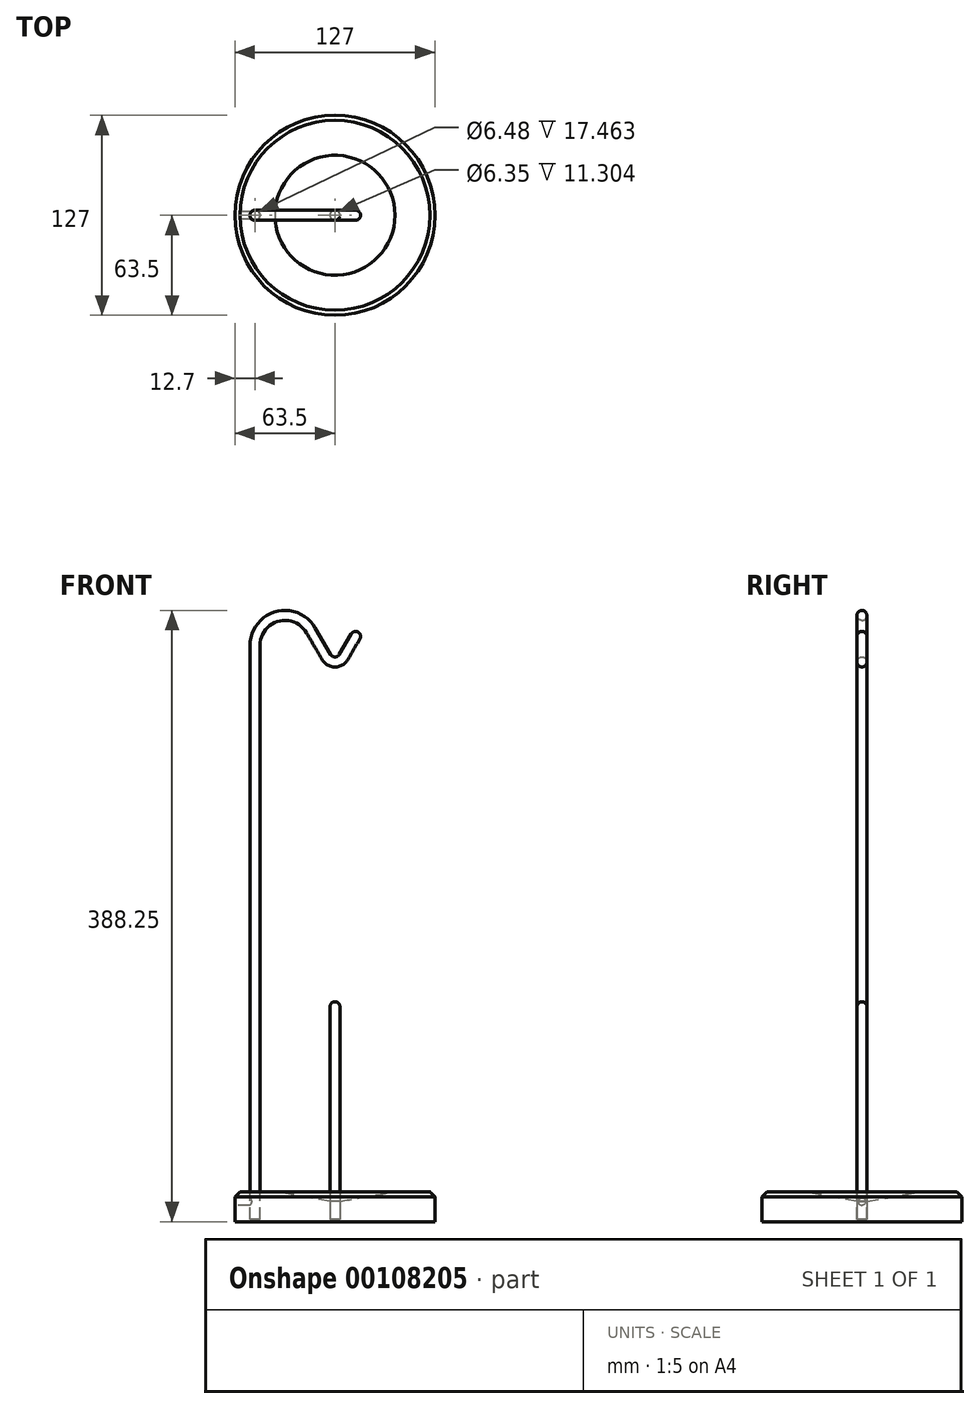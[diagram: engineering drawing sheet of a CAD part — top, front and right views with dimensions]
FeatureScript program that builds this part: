
annotation { "Feature Type Name" : "Feature", "Feature Type Description" : "" }
export const myFeature = defineFeature(function(context is Context, id is Id, definition is map)
    precondition{}
    {
        {
            var Q0;
            Q0=qCreatedBy(makeId("Front.planeOp"),FACE);
            var sketch = newSketch(context, id + "F0", { "sketchPlane" : qUnion([Q0])});
            skLineSegment(sketch, "E0", {"start": v(0, 0) * mm, "end": v(-63.5, 0) * mm});
            skLineSegment(sketch, "E1", {"start": v(-63.5, 0) * mm, "end": v(-63.5, 15.88) * mm});
            skLineSegment(sketch, "E2", {"start": v(-60.33, 19.05) * mm, "end": v(0, 19.05) * mm});
            skLineSegment(sketch, "E3", {"start": v(0, 19.05) * mm, "end": v(0, 0) * mm});
            skLineSegment(sketch, "E4", {"start": v(0, 12.33) * mm, "end": v(-38.1, 19.05) * mm});
            skLineSegment(sketch, "E5", {"start": v(0, 43.2) * mm, "end": v(0, -28.1) * mm, "construction": true});
            skPoint(sketch, "E5.endSnap0", {"position": v(0, 9.52) * mm});
            skLineSegment(sketch, "E6", {"start": v(-50.8, 40.56) * mm, "end": v(-50.8, -18.61) * mm, "construction": true});
            skLineSegment(sketch, "E7", {"start": v(-3.18, 19.05) * mm, "end": v(-3.17, 0) * mm, "construction": true});
            skLineSegment(sketch, "E8", {"start": v(-63.5, 15.88) * mm, "end": v(-60.33, 19.05) * mm});
            skLineSegment(sketch, "E9", {"start": v(-63.5, 0) * mm, "end": v(-63.5, 34.42) * mm, "construction": true});
            skSolve(sketch);
        }
        {
            var Q0;
            Q0=makeQuery(id+"F0.imprint","IMPRINT",FACE,{"disambiguationData":[TD([[makeQuery(id+"F0.imprint","IMPRINT",EDGE,{"derivedFrom":sQuery(id+"F0.wireOp",EDGE,"E0")}),-1.0]])]});
            var Q1;
            Q1=sQuery(id+"F0.wireOp",EDGE,"E3");
            revolve(context, id + "F1", {"entities" : qUnion([Q0]), "axis" : qUnion([Q1]), "revolveType" : RevolveType.FULL});
        }
        {
            var Q0;
            Q0=makeQuery(id+"F1.opRevolve","SWEPT_FACE",FACE,{"disambiguationData":[OSD([sQuery(id+"F0.wireOp",EDGE,"E2")])]});
            var sketch = newSketch(context, id + "F2", { "sketchPlane" : qUnion([Q0])});
            skLineSegment(sketch, "E10", {"start": v(81.4, 0) * mm, "end": v(-78.6, 0) * mm, "construction": true});
            skCircle(sketch, "E11", {"center": v(-50.8, 0) * mm, "radius": 3.24 * mm});
            skSolve(sketch);
        }
        {
            var Q0;
            Q0=makeQuery(id+"F2.imprint","IMPRINT",FACE,{"disambiguationData":[TD([[makeQuery(id+"F2.imprint","IMPRINT",EDGE,{"derivedFrom":sQuery(id+"F2.wireOp",EDGE,"E11")}),1.0]])]});
            extrude(context, id + "F3", {"entities" : qUnion([Q0]), "operationType" : NewBodyOperationType.REMOVE, "oppositeDirection" : true, "depth" : 17.46 * mm});
        }
        {
            var Q0;
            Q0=qCreatedBy(makeId("Top.planeOp"),FACE);
            var sketch = newSketch(context, id + "F4", { "sketchPlane" : qUnion([Q0])});
            skCircle(sketch, "E12", {"center": v(0, 0) * mm, "radius": 3.18 * mm});
            skSolve(sketch);
        }
        {
            var Q0;
            Q0 = qSketchRegion(id + "F4", true);
            extrude(context, id + "F5", {"entities" : qUnion([Q0]), "operationType" : NewBodyOperationType.REMOVE, "depth" : 15.24 * mm, "hasSecondDirection" : true, "secondDirectionOppositeDirection" : false, "secondDirectionDepth" : 1.59 * mm});
        }
        {
            var Q0;
            Q0=qCreatedBy(makeId("Top.planeOp"),FACE);
            var sketch = newSketch(context, id + "F6", { "sketchPlane" : qUnion([Q0])});
            skCircle(sketch, "E13", {"center": v(0, 0.01) * mm, "radius": 3.18 * mm});
            skSolve(sketch);
        }
        {
            var Q0;
            Q0 = qSketchRegion(id + "F6", true);
            extrude(context, id + "F7", {"entities" : qUnion([Q0]), "depth" : 139.7 * mm, "hasSecondDirection" : true, "secondDirectionOppositeDirection" : false, "secondDirectionDepth" : 1.59 * mm});
        }
        {
            var Q0;
            Q0=qCreatedBy(makeId("Right.planeOp"),FACE);
            cPlane(context, id + "F8", {"entities" : qUnion([Q0]), "cplaneType" : CPlaneType.OFFSET, "offset" : 63.5 * mm, "oppositeDirection" : true, "width" : 152.4 * mm, "height" : 152.4 * mm});
        }
        {
            var Q0;
            Q0=qCreatedBy(id+"F8.planeOp",FACE);
            var sketch = newSketch(context, id + "F9", { "sketchPlane" : qUnion([Q0])});
            skCircle(sketch, "E14", {"center": v(0, 12.7) * mm, "radius": 2.38 * mm});
            skSolve(sketch);
        }
        {
            var Q0;
            Q0 = qSketchRegion(id + "F9", true);
            extrude(context, id + "F10", {"entities" : qUnion([Q0]), "operationType" : NewBodyOperationType.REMOVE, "depth" : 12.7 * mm});
        }
        {
            var Q0;
            Q0=qCreatedBy(makeId("Front.planeOp"),FACE);
            var sketch = newSketch(context, id + "F11", { "sketchPlane" : qUnion([Q0])});
            skLineSegment(sketch, "E15", {"start": v(-50.8, 1.59) * mm, "end": v(-50.8, 366.03) * mm});
            skLineSegment(sketch, "E16", {"start": v(5.5, 358.66) * mm, "end": v(14.66, 374.54) * mm});
            skLineSegment(sketch, "E17", {"start": v(-5.5, 358.66) * mm, "end": v(-15.25, 375.55) * mm});
            skPoint(sketch, "E18.visualSharp", {"position": v(0, 349.14) * mm});
            skArc(sketch, "E18.filletArc", {"start": v(-5.5, 358.66) * mm, "mid": v(0, 355.49) * mm, "end": v(5.5, 358.66) * mm});
            skPoint(sketch, "E19.visualSharp", {"position": v(-50.8, 437.12) * mm});
            skArc(sketch, "E19.filletArc", {"start": v(-15.25, 375.55) * mm, "mid": v(-36.68, 384.43) * mm, "end": v(-50.8, 366.03) * mm});
            skSolve(sketch);
        }
        {
            var Q0;
            Q0=makeQuery(id+"F3.boolean.opBoolean","COPY",FACE,{"derivedFrom":makeQuery(id+"F3.opExtrude","CAP_FACE",FACE,{"disambiguationData":[OSD([sQuery(id+"F2.wireOp",EDGE,"E11")])],"isStart":false})});
            var sketch = newSketch(context, id + "F12", { "sketchPlane" : qUnion([Q0])});
            skCircle(sketch, "E20", {"center": v(-50.8, 0) * mm, "radius": 3.18 * mm});
            skSolve(sketch);
        }
        {
            var Q0;
            Q0 = qSketchRegion(id + "F12", true);
            var Q1;
            Q1 = qConstructionFilter(qBodyType(qCreatedBy(id + "F11" ,EDGE), BodyType.WIRE), ConstructionObject.NO);
            sweep(context, id + "F13", {"profiles" : qUnion([Q0]), "path" : qUnion([Q1])});
        }
        {
            var Q0;
            Q0=makeQuery(id+"F7.opExtrude","CAP_FACE",FACE,{"disambiguationData":[OSD([sQuery(id+"F6.wireOp",EDGE,"E13")])],"isStart":false});
            var Q1;
            Q1=makeQuery(id+"F13.opSweep","CAP_EDGE",EDGE,{"disambiguationData":[OSD([sQuery(id+"F11.wireOp",VERTEX,"E16.end"),sQuery(id+"F12.wireOp",EDGE,"E20")])],"isStart":false});
            fillet(context, id + "F14", {"entities" : qUnion([Q0, Q1]), "radius" : 3.17 * mm, "tangentPropagation" : true, "allowEdgeOverflow" : false});
        }
    });
